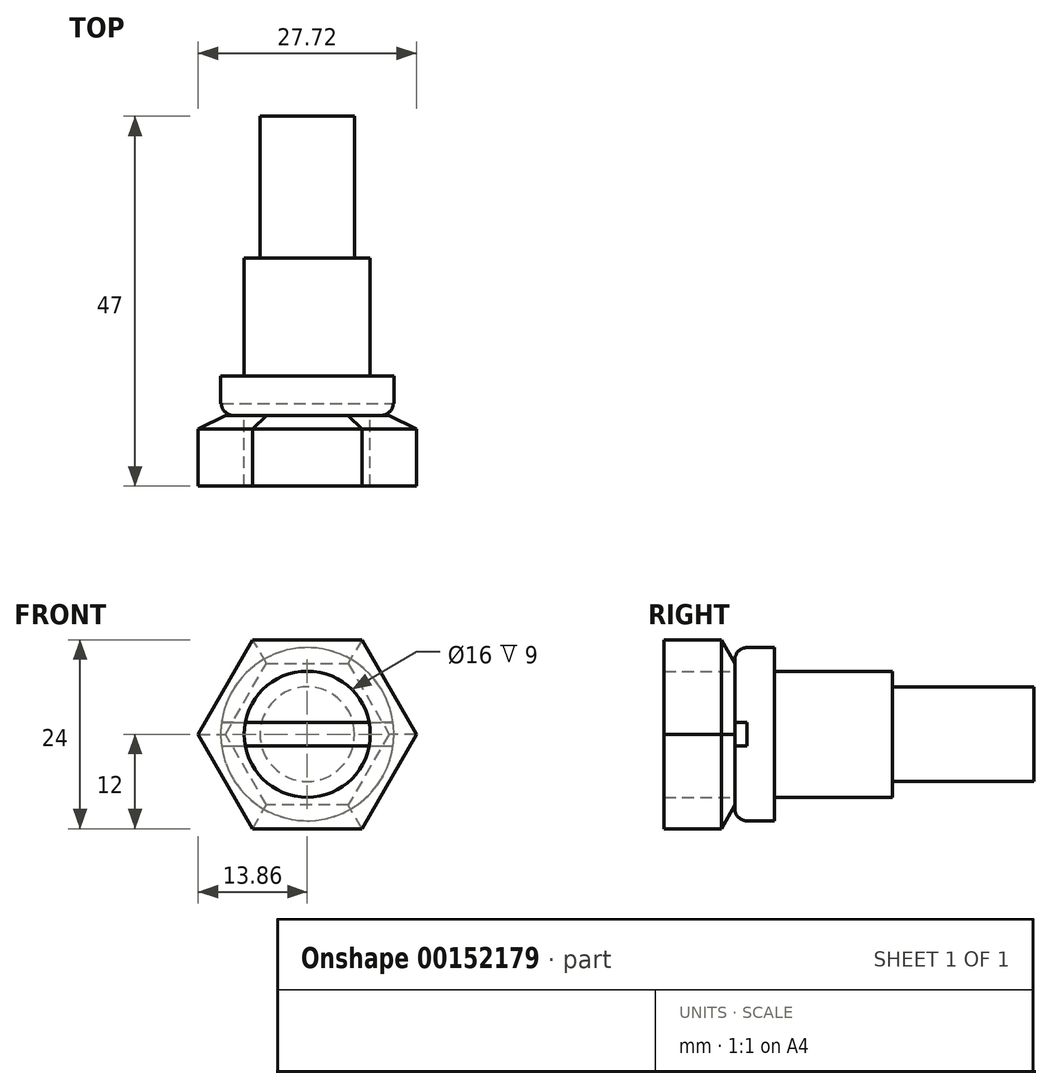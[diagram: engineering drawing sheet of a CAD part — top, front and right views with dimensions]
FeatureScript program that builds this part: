
annotation { "Feature Type Name" : "Feature", "Feature Type Description" : "" }
export const myFeature = defineFeature(function(context is Context, id is Id, definition is map)
    precondition{}
    {
        {
            var Q0;
            Q0=qCreatedBy(makeId("Right.planeOp"),FACE);
            var sketch = newSketch(context, id + "F0", { "sketchPlane" : qUnion([Q0])});
            skLineSegment(sketch, "E0", {"start": v(-23.21, 0) * mm, "end": v(51.1, 0) * mm, "construction": true});
            skLineSegment(sketch, "E1", {"start": v(0, 0) * mm, "end": v(0, 11) * mm});
            skLineSegment(sketch, "E2", {"start": v(0, 11) * mm, "end": v(5, 11) * mm});
            skLineSegment(sketch, "E3", {"start": v(5, 11) * mm, "end": v(5, 8) * mm});
            skLineSegment(sketch, "E4", {"start": v(5, 8) * mm, "end": v(20, 8) * mm});
            skLineSegment(sketch, "E5", {"start": v(20, 8) * mm, "end": v(20, 8) * mm});
            skLineSegment(sketch, "E6", {"start": v(38, 6) * mm, "end": v(38, 0) * mm});
            skLineSegment(sketch, "E7", {"start": v(38, 0) * mm, "end": v(0, 0) * mm});
            skLineSegment(sketch, "E8", {"start": v(20, 18.17) * mm, "end": v(20, -6.86) * mm, "construction": true});
            skPoint(sketch, "E9", {"position": v(20, 8) * mm});
            skLineSegment(sketch, "E10", {"start": v(38, 6) * mm, "end": v(20, 6) * mm});
            skLineSegment(sketch, "E11", {"start": v(20, 6) * mm, "end": v(20, 8) * mm});
            skSolve(sketch);
        }
        {
            var Q0;
            Q0=makeQuery(id+"F0.imprint","IMPRINT",FACE,{"disambiguationData":[TD([[makeQuery(id+"F0.imprint","IMPRINT",EDGE,{"derivedFrom":sQuery(id+"F0.wireOp",EDGE,"E1")}),-1.0]])]});
            var Q1;
            Q1=sQuery(id+"F0.wireOp",EDGE,"E0");
            revolve(context, id + "F1", {"entities" : qUnion([Q0]), "axis" : qUnion([Q1]), "revolveType" : RevolveType.FULL});
        }
        {
            var Q0;
            Q0=qCreatedBy(makeId("Front.planeOp"),FACE);
            var sketch = newSketch(context, id + "F2", { "sketchPlane" : qUnion([Q0])});
            skCircle(sketch, "E12.cCircle", {"center": v(0, 0) * mm, "radius": 12 * mm, "construction": true});
            skLineSegment(sketch, "E12.0", {"start": v(6.93, -12) * mm, "end": v(-6.93, -12) * mm});
            skLineSegment(sketch, "E12.1", {"start": v(-6.93, -12) * mm, "end": v(-13.86, 0) * mm});
            skLineSegment(sketch, "E12.2", {"start": v(-13.86, 0) * mm, "end": v(-6.93, 12) * mm});
            skLineSegment(sketch, "E12.3", {"start": v(-6.93, 12) * mm, "end": v(6.93, 12) * mm});
            skLineSegment(sketch, "E12.4", {"start": v(6.93, 12) * mm, "end": v(13.86, 0) * mm});
            skLineSegment(sketch, "E12.5", {"start": v(13.86, 0) * mm, "end": v(6.93, -12) * mm});
            skPoint(sketch, "E12.0.midPoint", {"position": v(0, -12) * mm});
            skCircle(sketch, "E13", {"center": v(0, 0) * mm, "radius": 8 * mm});
            skSolve(sketch);
        }
        {
            var Q0;
            Q0=qSketchRegion(id+"F2",true);
            extrude(context, id + "F3", {"entities" : qUnion([Q0]), "depth" : 9 * mm});
        }
        {
            var Q0;
            Q0=makeQuery(id+"F1.opRevolve","SWEPT_FACE",FACE,{"disambiguationData":[OSD([sQuery(id+"F0.wireOp",EDGE,"E1")])]});
            var sketch = newSketch(context, id + "F4", { "sketchPlane" : qUnion([Q0])});
            skLineSegment(sketch, "E14.bottom", {"start": v(-12.04, 1.5) * mm, "end": v(12.96, 1.5) * mm});
            skLineSegment(sketch, "E14.top", {"start": v(-12.04, -1.5) * mm, "end": v(12.96, -1.5) * mm});
            skLineSegment(sketch, "E14.left", {"start": v(-12.04, 1.5) * mm, "end": v(-12.04, -1.5) * mm});
            skLineSegment(sketch, "E14.right", {"start": v(12.96, 1.5) * mm, "end": v(12.96, -1.5) * mm});
            skSolve(sketch);
        }
        {
            var Q0;
            Q0=qSketchRegion(id+"F4",true);
            extrude(context, id + "F5", {"entities" : qUnion([Q0]), "operationType" : NewBodyOperationType.REMOVE, "oppositeDirection" : true, "depth" : 1.5 * mm});
        }
        {
            var Q0;
            {var subQ0=sQuery(id+"F0.wireOp",EDGE,"E1");var subQ1=sQuery(id+"F0.wireOp",EDGE,"E2");Q0=makeQuery(id+"F5.boolean.opBoolean","SPLIT",EDGE,{"disambiguationData":[TD([makeQuery(id+"F5.opExtrude","SWEPT_FACE",FACE,{"disambiguationData":[OSD([sQuery(id+"F4.wireOp",EDGE,"E14.bottom")])]})])],"derivedFrom":makeQuery(id+"F1.opRevolve","SWEPT_EDGE",EDGE,{"disambiguationData":[OSD([subQ0,subQ1])]})});}
            var Q1;
            {var subQ0=sQuery(id+"F0.wireOp",EDGE,"E1");var subQ1=sQuery(id+"F0.wireOp",EDGE,"E2");Q1=makeQuery(id+"F5.boolean.opBoolean","SPLIT",EDGE,{"disambiguationData":[TD([makeQuery(id+"F5.opExtrude","SWEPT_FACE",FACE,{"disambiguationData":[OSD([sQuery(id+"F4.wireOp",EDGE,"E14.top")])]})])],"derivedFrom":makeQuery(id+"F1.opRevolve","SWEPT_EDGE",EDGE,{"disambiguationData":[OSD([subQ0,subQ1])]})});}
            fillet(context, id + "F6", {"entities" : qUnion([Q0, Q1]), "radius" : 1.5 * mm, "tangentPropagation" : true, "allowEdgeOverflow" : false});
        }
        {
            var Q0;
            Q0=makeQuery(id+"F3.opExtrude","CAP_EDGE",EDGE,{"disambiguationData":[OSD([sQuery(id+"F2.wireOp",EDGE,"E12.3")])],"isStart":true});
            var Q1;
            Q1=makeQuery(id+"F3.opExtrude","CAP_EDGE",EDGE,{"disambiguationData":[OSD([sQuery(id+"F2.wireOp",EDGE,"E12.4")])],"isStart":true});
            var Q2;
            Q2=makeQuery(id+"F3.opExtrude","CAP_EDGE",EDGE,{"disambiguationData":[OSD([sQuery(id+"F2.wireOp",EDGE,"E12.5")])],"isStart":true});
            var Q3;
            Q3=makeQuery(id+"F3.opExtrude","CAP_EDGE",EDGE,{"disambiguationData":[OSD([sQuery(id+"F2.wireOp",EDGE,"E12.0")])],"isStart":true});
            var Q4;
            Q4=makeQuery(id+"F3.opExtrude","CAP_EDGE",EDGE,{"disambiguationData":[OSD([sQuery(id+"F2.wireOp",EDGE,"E12.1")])],"isStart":true});
            var Q5;
            Q5=makeQuery(id+"F3.opExtrude","CAP_EDGE",EDGE,{"disambiguationData":[OSD([sQuery(id+"F2.wireOp",EDGE,"E12.2")])],"isStart":true});
            chamfer(context, id + "F7", {"entities" : qUnion([Q0, Q1, Q2, Q3, Q4, Q5]), "chamferType" : ChamferType.OFFSET_ANGLE, "width" : 3 * mm, "oppositeDirection" : false, "angle" : 30 * degree, "tangentPropagation" : true});
        }
    });
